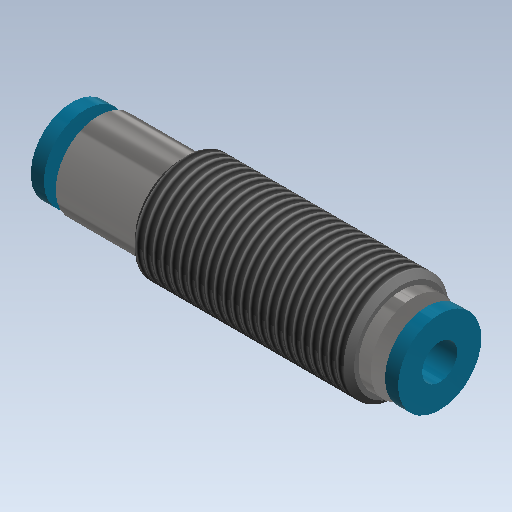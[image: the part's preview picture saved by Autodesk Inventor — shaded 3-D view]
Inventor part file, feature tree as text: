
AUTODESK INVENTOR PART (.ipt)
format: ipt  version: 2021 (Build 250183000, 183)  size: 187,904 bytes
history: native  units: mm (DEFAULTED — no unit token found)
features: other x21, revolve x1, thread x1, sketch x1
ambient origin geometry x8: Origin, YZ Plane, XZ Plane, XY Plane, X Axis, Y Axis, Z Axis, Center Point
bodies: Solid1 (feature_tree)
feature tree (24):
  revolve  "Revolution1"  [1 undecoded]
  thread  "Thread1"  [1 undecoded]
  other  "IP1_XY"
  other  "IP1_YZ"
  other  "IP1_ZX"
  other  "IP1_X"
  other  "IP1_Y"
  other  "IP1_Z"
  other  "IP1_Center"
  other  "IP2_XY"
  other  "IP2_YZ"
  other  "IP2_ZX"
  other  "IP2_X"
  other  "IP2_Y"
  other  "IP2_Z"
  other  "IP2_Center"
  other  "IP3_XY"
  other  "IP3_YZ"
  other  "IP3_ZX"
  other  "IP3_X"
  other  "IP3_Y"
  other  "IP3_Z"
  other  "IP3_Center"
  sketch  "Sketch_1"  dims[d0=360.0deg d1=23.873mm d2=0.0mm d3=0.0mm]
note: 2 required parameter values undecoded (feature->parameter linkage not recoverable at this tier; creation-order binding heuristic only, values carry confidence <= 0.55)